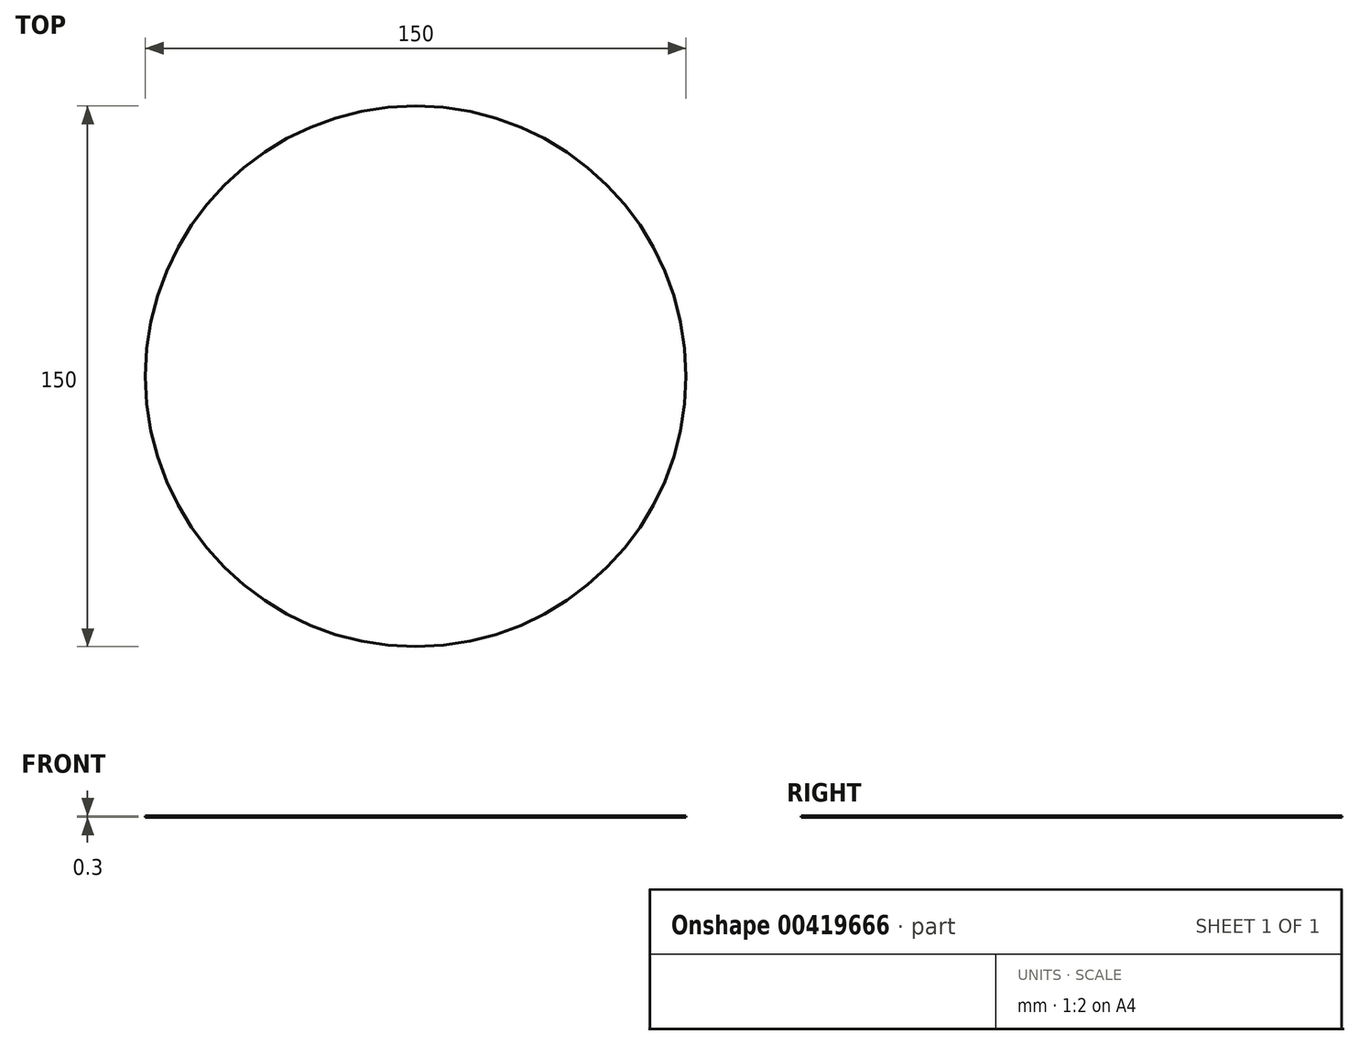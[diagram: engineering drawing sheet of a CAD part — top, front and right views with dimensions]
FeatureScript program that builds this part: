
annotation { "Feature Type Name" : "Feature", "Feature Type Description" : "" }
export const myFeature = defineFeature(function(context is Context, id is Id, definition is map)
    precondition{}
    {
        {
            var Q0;
            Q0=qCreatedBy(makeId("Top.planeOp"),FACE);
            var sketch = newSketch(context, id + "F0", { "sketchPlane" : qUnion([Q0])});
            skCircle(sketch, "E0", {"center": v(0, 0) * mm, "radius": 75 * mm});
            skSolve(sketch);
        }
        {
            var Q0;
            Q0=makeQuery(id+"F0.imprint","IMPRINT",FACE,{"disambiguationData":[TD([[makeQuery(id+"F0.imprint","IMPRINT",EDGE,{"derivedFrom":sQuery(id+"F0.wireOp",EDGE,"E0")}),1.0]])]});
            extrude(context, id + "F1", {"entities" : qUnion([Q0]), "depth" : .3 * mm});
        }
    });
